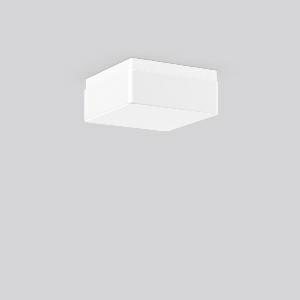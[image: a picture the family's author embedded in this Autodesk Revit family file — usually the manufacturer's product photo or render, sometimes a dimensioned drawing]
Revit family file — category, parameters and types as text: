
# Revit family: quadrat_20172_002_1df6
name_source: partatom
category: Lighting Fixtures
units: mm (PartAtom-declared; Revit-internal decimal feet)

## family parameters
Cut with Voids When Loaded = No
Host = Face
Light Source = No
Part Type = Normal
Room Calculation Point = No
Round Connector Dimension = Use Diameter
Shared = No

## types (1)
- QUADRAT (1 x QA60/clear E27, 1320 lm, 77 W, 3000)
    Apparent Load = 77 VA
    CIE Flux Codes = 34 63 85 72 42
    Color Rendering = 90
    Color Temperature = 3000
    Default Elevation = 1800 mm
    Description = Series: QUADRAT
Square surface-mounted luminaire in classic design. Base: plastic. Opal glass: mouth blown, silk finish. Diffuser fastening: spring system. Suitable for Ceiling mounting, Wall (surface). IP 43 ceiling mounting, IP 44 wall mounting. 
Colour: white
Length: 280 mm
Width: 280 mm
Height: 120 mm
Lamp: A60
Number of lamps: 1
Wattage: 100 W
Socket: E27
System power: 60 W
Rated luminous flux: 310 lm
Luminous efficiency: 5 lm/W
Control gear: Converter not necessary
Protection class: II
Type of protection: IP 43
    Height = 120 mm
    Lamp = 1 x QA60/clear E27
    Lamp Light Flux = 1320 lm
    Lamp Power = 77 W
    Lamp count = 1
    Length = 280 mm
    Lifetime = 3000 h
    Luminous efficacy = 7 lm/W
    Manufacturer = RZB
    ModVariant = No
    Model = 20172.002
    Mounting Place = Ceiling, Wall
    Mounting Type = Surface mounted
    Number of Poles = 1
    OnlyDefault = Yes
    Power Factor = 1
    Product Name = QUADRAT
    Product group = Surface mounted ceiling and wall luminaires
    ProductGroupID = 305
    Protection Class = Protection class II
    Protection Degree = IP 43
    RLX_Detail_Level = 1
    RLX_Emergency_Light_Flux = 0 lm
    RLX_Emergency_Type = 0
    RLX_Emergency_Type_DB = No
    RlxData = <blob elided: 11333 chars, md5=af0d4038>
    Socket = E27
    Standby Power = 0 W
    System Light Flux = 558 lm
    System Power = 77 W
    Type Comments = Product without accessories
    Type Image = 20129.002.jpg
    URL = http://relux.com
    VarID = ---
    Voltage = 230 V
    Voltage Range = 220-240 V
    Weight = 0.00 kg
    Width = 280 mm

## geometry (parser evidence)
native form markers: Sweep x13
no freeform markers — native parametric forms only
